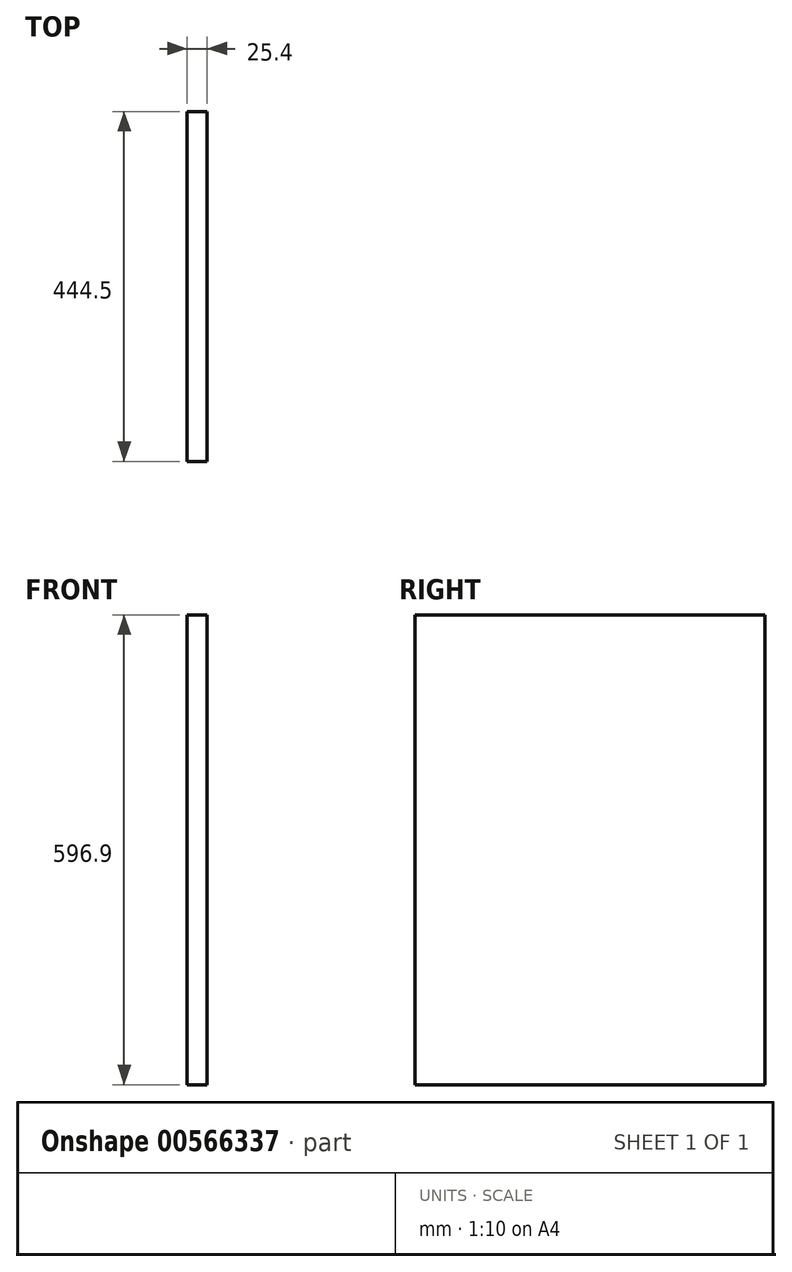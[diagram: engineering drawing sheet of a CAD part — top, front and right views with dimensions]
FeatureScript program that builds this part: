
annotation { "Feature Type Name" : "Feature", "Feature Type Description" : "" }
export const myFeature = defineFeature(function(context is Context, id is Id, definition is map)
    precondition{}
    {
        {
            var Q0;
            Q0=qCreatedBy(makeId("Right.planeOp"),FACE);
            var sketch = newSketch(context, id + "F0", { "sketchPlane" : qUnion([Q0])});
            skLineSegment(sketch, "E0.bottom", {"start": v(-406.4, 0) * mm, "end": v(0, 0) * mm});
            skLineSegment(sketch, "E0.top", {"start": v(-406.4, 558.8) * mm, "end": v(0, 558.8) * mm});
            skLineSegment(sketch, "E0.left", {"start": v(0, 0) * mm, "end": v(0, 558.8) * mm});
            skLineSegment(sketch, "E0.right", {"start": v(-406.4, 0) * mm, "end": v(-406.4, 558.8) * mm});
            skSolve(sketch);
        }
        {
            var Q0;
            Q0=qCreatedBy(makeId("Right.planeOp"),FACE);
            var sketch = newSketch(context, id + "F1", { "sketchPlane" : qUnion([Q0])});
            skLineSegment(sketch, "E1.bottom", {"start": v(-6.35, 6.35) * mm, "end": v(-400.05, 6.35) * mm});
            skLineSegment(sketch, "E1.top", {"start": v(-6.35, 552.45) * mm, "end": v(-400.05, 552.45) * mm});
            skLineSegment(sketch, "E1.left", {"start": v(-6.35, 6.35) * mm, "end": v(-6.35, 552.45) * mm});
            skLineSegment(sketch, "E1.right", {"start": v(-400.05, 6.35) * mm, "end": v(-400.05, 552.45) * mm});
            skSolve(sketch);
        }
        {
            var Q0;
            Q0=qCreatedBy(makeId("Right.planeOp"),FACE);
            var sketch = newSketch(context, id + "F2", { "sketchPlane" : qUnion([Q0])});
            skLineSegment(sketch, "E2.bottom", {"start": v(19.05, -19.05) * mm, "end": v(-425.45, -19.05) * mm});
            skLineSegment(sketch, "E2.top", {"start": v(19.05, 577.85) * mm, "end": v(-425.45, 577.85) * mm});
            skLineSegment(sketch, "E2.left", {"start": v(19.05, -19.05) * mm, "end": v(19.05, 577.85) * mm});
            skLineSegment(sketch, "E2.right", {"start": v(-425.45, -19.05) * mm, "end": v(-425.45, 577.85) * mm});
            skSolve(sketch);
        }
        {
            var Q0;
            Q0=makeQuery(id+"F2.imprint","IMPRINT",FACE,{"disambiguationData":[TD([[makeQuery(id+"F2.imprint","IMPRINT",EDGE,{"derivedFrom":sQuery(id+"F2.wireOp",EDGE,"E2.bottom")}),-1.0]])]});
            extrude(context, id + "F3", {"entities" : qUnion([Q0]), "depth" : 25.4 * mm, "offsetDistance" : 25.4 * mm});
        }
        {
            var Q0;
            Q0=makeQuery(id+"F1.imprint","IMPRINT",FACE,{"disambiguationData":[TD([[makeQuery(id+"F1.imprint","IMPRINT",EDGE,{"derivedFrom":sQuery(id+"F1.wireOp",EDGE,"E1.bottom")}),-1.0]])]});
            extrude(context, id + "F4", {"entities" : qUnion([Q0]), "operationType" : NewBodyOperationType.ADD, "depth" : 25.4 * mm, "offsetDistance" : 25.4 * mm});
        }
    });
